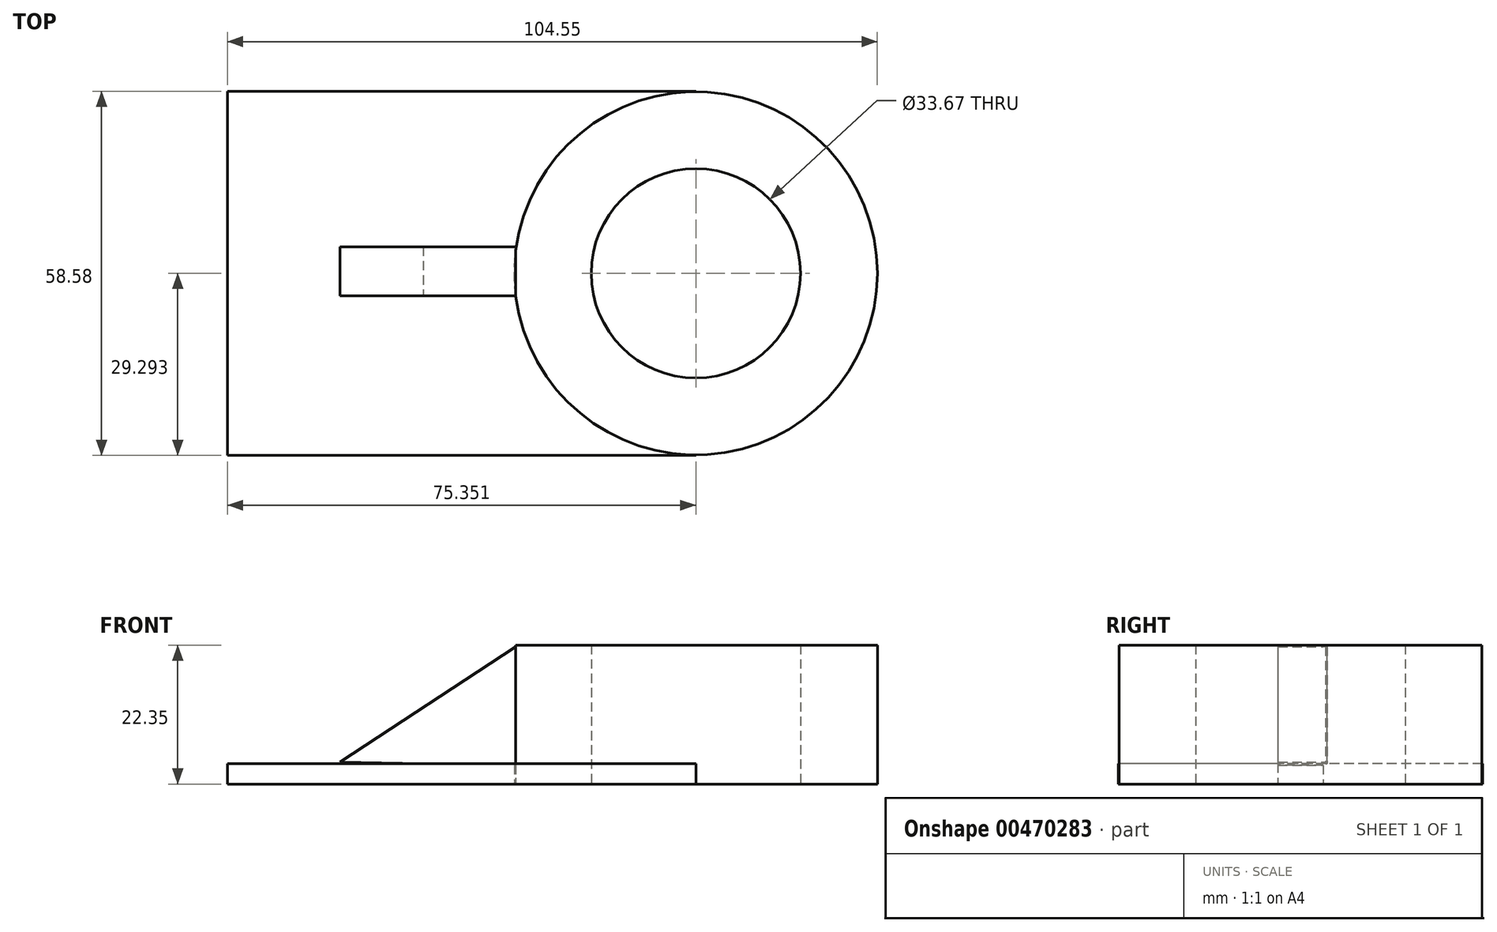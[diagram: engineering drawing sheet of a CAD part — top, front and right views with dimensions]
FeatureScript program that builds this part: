
annotation { "Feature Type Name" : "Feature", "Feature Type Description" : "" }
export const myFeature = defineFeature(function(context is Context, id is Id, definition is map)
    precondition{}
    {
        {
            var Q0;
            Q0=qCreatedBy(makeId("Top.planeOp"),FACE);
            var sketch = newSketch(context, id + "F0", { "sketchPlane" : qUnion([Q0])});
            skLineSegment(sketch, "E0.bottom", {"start": v(-94.25, 17.64) * mm, "end": v(-18.9, 17.64) * mm});
            skLineSegment(sketch, "E0.top", {"start": v(-94.25, -40.94) * mm, "end": v(-18.9, -40.94) * mm});
            skLineSegment(sketch, "E0.left", {"start": v(-94.25, 17.64) * mm, "end": v(-94.25, -40.94) * mm});
            skLineSegment(sketch, "E0.right", {"start": v(-18.9, 17.64) * mm, "end": v(-18.9, -40.94) * mm});
            skCircle(sketch, "E1", {"center": v(-18.9, -11.65) * mm, "radius": 29.2 * mm});
            skCircle(sketch, "E2", {"center": v(-18.9, -11.65) * mm, "radius": 16.83 * mm});
            skLineSegment(sketch, "E3.bottom", {"start": v(-47.87, -15.31) * mm, "end": v(-76.08, -15.31) * mm});
            skLineSegment(sketch, "E3.top", {"start": v(-47.87, -6.9) * mm, "end": v(-76.08, -6.9) * mm});
            skLineSegment(sketch, "E3.left", {"start": v(-47.87, -15.31) * mm, "end": v(-47.87, -6.9) * mm});
            skLineSegment(sketch, "E3.right", {"start": v(-76.08, -15.31) * mm, "end": v(-76.08, -6.9) * mm});
            skSolve(sketch);
        }
        {
            var Q0;
            {var subQ0=sQuery(id+"F0.wireOp",EDGE,"E1");var subQ1=sQuery(id+"F0.wireOp",EDGE,"E0.right");var subQ2=makeQuery(id+"F0.imprint","INTERSECT",VERTEX,{"disambiguationData":[OD(0.0)],"derivedFrom":[subQ1,subQ0]});Q0=makeQuery(id+"F0.imprint","IMPRINT",FACE,{"disambiguationData":[TD([[makeQuery(id+"F0.imprint","IMPRINT",EDGE,{"disambiguationData":[TD([[subQ2,-1.0]])],"derivedFrom":subQ1}),1.0]])]});}
            var Q1;
            {var subQ1=sQuery(id+"F0.wireOp",EDGE,"E1");var subQ3=sQuery(id+"F0.wireOp",EDGE,"E0.right");var subQ5=makeQuery(id+"F0.imprint","INTERSECT",VERTEX,{"disambiguationData":[OD(0.0)],"derivedFrom":[subQ3,subQ1]});Q1=makeQuery(id+"F0.imprint","IMPRINT",FACE,{"disambiguationData":[TD([[makeQuery(id+"F0.imprint","IMPRINT",EDGE,{"disambiguationData":[TD([[subQ5,-1.0]])],"derivedFrom":subQ3}),-1.0]])]});}
            extrude(context, id + "F1", {"entities" : qUnion([Q0, Q1]), "depth" : 22.35 * mm});
        }
        {
            var Q0;
            {var subQ9=sQuery(id+"F0.wireOp",EDGE,"E0.bottom");Q0=makeQuery(id+"F0.imprint","IMPRINT",FACE,{"disambiguationData":[TD([[makeQuery(id+"F0.imprint","IMPRINT",EDGE,{"derivedFrom":subQ9}),-1.0]])]});}
            var Q1;
            {var subQ4=sQuery(id+"F0.wireOp",EDGE,"E3.bottom");Q1=makeQuery(id+"F0.imprint","IMPRINT",FACE,{"disambiguationData":[TD([[makeQuery(id+"F0.imprint","IMPRINT",EDGE,{"derivedFrom":subQ4}),-1.0]])]});}
            extrude(context, id + "F2", {"entities" : qUnion([Q0, Q1]), "operationType" : NewBodyOperationType.ADD, "depth" : 3.3 * mm});
        }
        {
            var Q0;
            Q0=qCreatedBy(makeId("Front.planeOp"),FACE);
            var sketch = newSketch(context, id + "F3", { "sketchPlane" : qUnion([Q0])});
            skLineSegment(sketch, "E4", {"start": v(-76.18, 3.54) * mm, "end": v(-47.82, 22.1) * mm});
            skLineSegment(sketch, "E5", {"start": v(-47.82, 22.1) * mm, "end": v(-47.82, 3.03) * mm});
            skLineSegment(sketch, "E6", {"start": v(-47.82, 3.03) * mm, "end": v(-76.18, 3.54) * mm});
            skSolve(sketch);
        }
        {
            var Q0;
            Q0=makeQuery(id+"F3.imprint","IMPRINT",FACE,{"disambiguationData":[TD([[makeQuery(id+"F3.imprint","IMPRINT",EDGE,{"derivedFrom":sQuery(id+"F3.wireOp",EDGE,"E4")}),-1.0]])]});
            extrude(context, id + "F4", {"entities" : qUnion([Q0]), "operationType" : NewBodyOperationType.ADD, "depth" : 15.24 * mm});
        }
        {
            var Q0;
            Q0=makeQuery(id+"F4.opExtrude","CAP_FACE",FACE,{"disambiguationData":[OSD([sQuery(id+"F3.wireOp",EDGE,"E4"),sQuery(id+"F3.wireOp",EDGE,"E5"),sQuery(id+"F3.wireOp",EDGE,"E6")])],"isStart":true});
            extrude(context, id + "F5", {"entities" : qUnion([Q0]), "operationType" : NewBodyOperationType.REMOVE, "oppositeDirection" : true, "depth" : 7.37 * mm});
        }
    });
